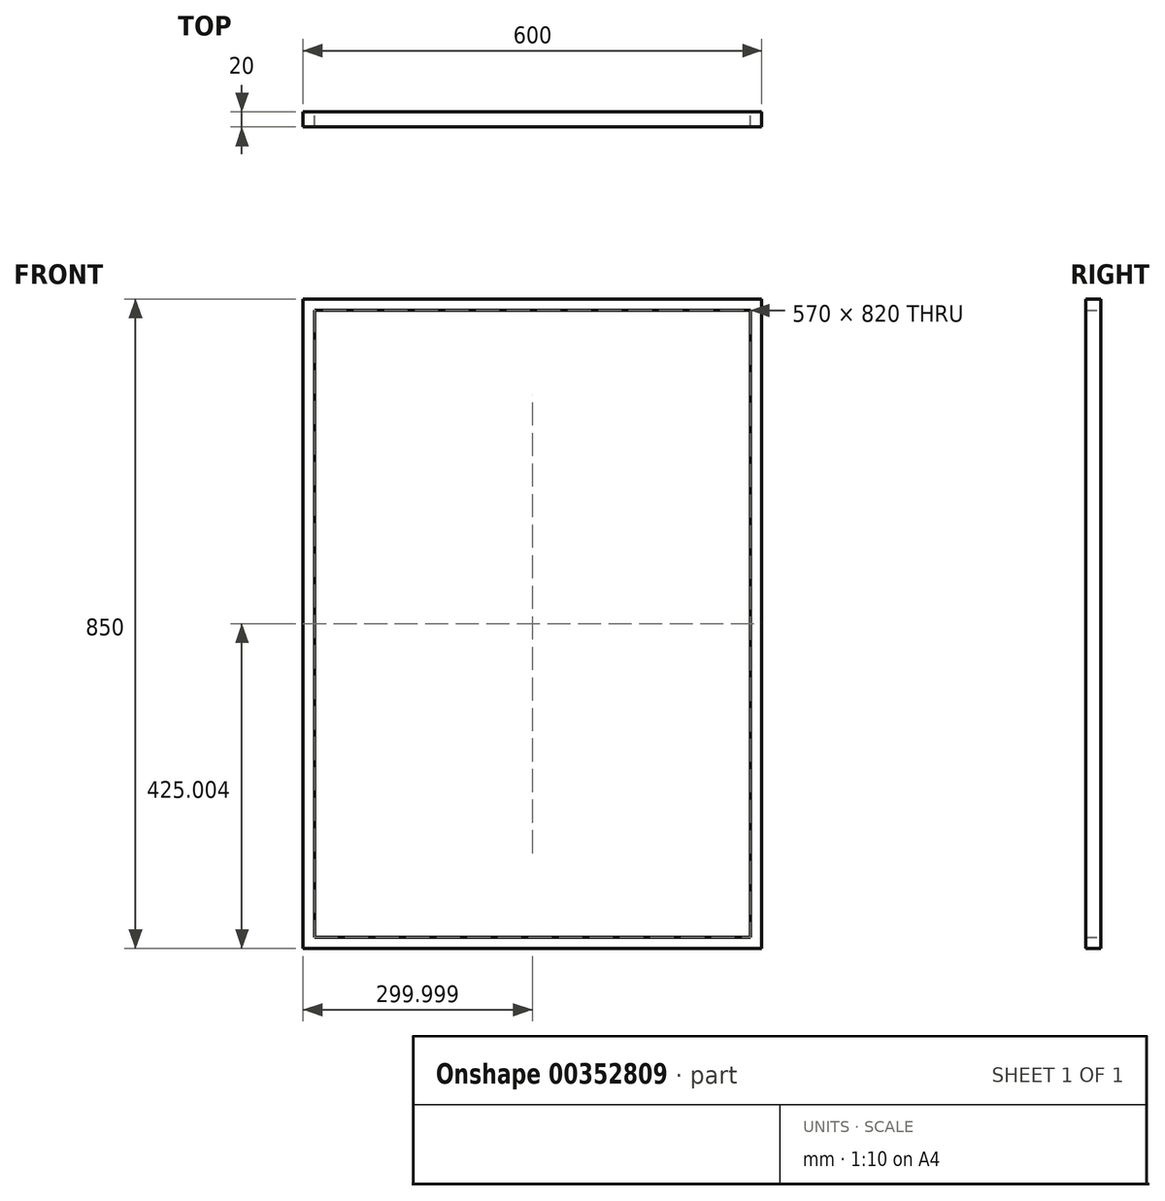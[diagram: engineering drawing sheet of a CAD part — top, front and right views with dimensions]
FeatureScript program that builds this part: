
annotation { "Feature Type Name" : "Feature", "Feature Type Description" : "" }
export const myFeature = defineFeature(function(context is Context, id is Id, definition is map)
    precondition{}
    {
        {
            var Q0;
            Q0=qCreatedBy(makeId("Front.planeOp"),FACE);
            var sketch = newSketch(context, id + "F0", { "sketchPlane" : qUnion([Q0])});
            skLineSegment(sketch, "E0.bottom", {"start": v(-39.41, 785.08) * mm, "end": v(560.59, 785.08) * mm});
            skLineSegment(sketch, "E0.top", {"start": v(-39.41, -64.92) * mm, "end": v(560.59, -64.92) * mm});
            skLineSegment(sketch, "E0.left", {"start": v(-39.41, 785.08) * mm, "end": v(-39.41, -64.92) * mm});
            skLineSegment(sketch, "E0.right", {"start": v(560.59, 785.08) * mm, "end": v(560.59, -64.92) * mm});
            skLineSegment(sketch, "E1.0", {"start": v(-24.41, 770.08) * mm, "end": v(545.59, 770.08) * mm});
            skLineSegment(sketch, "E1.1", {"start": v(-24.41, 770.08) * mm, "end": v(-24.41, -49.92) * mm});
            skLineSegment(sketch, "E1.2", {"start": v(-24.41, -49.92) * mm, "end": v(545.59, -49.92) * mm});
            skLineSegment(sketch, "E1.3", {"start": v(545.59, 770.08) * mm, "end": v(545.59, -49.92) * mm});
            skSolve(sketch);
        }
        {
            var Q0;
            Q0=qSketchRegion(id+"F0",true);
            extrude(context, id + "F1", {"entities" : qUnion([Q0]), "depth" : 20 * mm});
        }
        {
            var Q0;
            Q0=makeQuery(id+"F1.opExtrude","CAP_FACE",FACE,{"disambiguationData":[OSD([sQuery(id+"F0.wireOp",EDGE,"E0.bottom"),sQuery(id+"F0.wireOp",EDGE,"E0.top"),sQuery(id+"F0.wireOp",EDGE,"E0.left"),sQuery(id+"F0.wireOp",EDGE,"E0.right"),sQuery(id+"F0.wireOp",EDGE,"E1.0"),sQuery(id+"F0.wireOp",EDGE,"E1.1"),sQuery(id+"F0.wireOp",EDGE,"E1.2"),sQuery(id+"F0.wireOp",EDGE,"E1.3")])],"isStart":false});
            var sketch = newSketch(context, id + "F2", { "sketchPlane" : qUnion([Q0])});
            skLineSegment(sketch, "E2.bottom", {"start": v(-39.41, 785.08) * mm, "end": v(560.59, 785.08) * mm});
            skLineSegment(sketch, "E2.top", {"start": v(-39.41, -64.92) * mm, "end": v(560.59, -64.92) * mm});
            skLineSegment(sketch, "E2.left", {"start": v(-39.41, 785.08) * mm, "end": v(-39.41, -64.92) * mm});
            skLineSegment(sketch, "E2.right", {"start": v(560.59, 785.08) * mm, "end": v(560.59, -64.92) * mm});
            skSolve(sketch);
        }
        {
            var Q0;
            Q0=qSketchRegion(id+"F2",true);
            extrude(context, id + "F3", {"entities" : qUnion([Q0]), "operationType" : NewBodyOperationType.ADD, "oppositeDirection" : true, "depth" : 5 * mm});
        }
        {
            var Q0;
            Q0=makeQuery(id+"F3.opExtrude","CAP_FACE",FACE,{"disambiguationData":[OSD([sQuery(id+"F2.wireOp",EDGE,"E2.bottom"),sQuery(id+"F2.wireOp",EDGE,"E2.top"),sQuery(id+"F2.wireOp",EDGE,"E2.left"),sQuery(id+"F2.wireOp",EDGE,"E2.right")])],"isStart":false});
            var sketch = newSketch(context, id + "F4", { "sketchPlane" : qUnion([Q0])});
            skLineSegment(sketch, "E3.bottom", {"start": v(-545.59, 770.08) * mm, "end": v(24.41, 770.08) * mm});
            skLineSegment(sketch, "E3.top", {"start": v(-545.59, -49.92) * mm, "end": v(24.41, -49.92) * mm});
            skLineSegment(sketch, "E3.left", {"start": v(-545.59, 770.08) * mm, "end": v(-545.59, -49.92) * mm});
            skLineSegment(sketch, "E3.right", {"start": v(24.41, 770.08) * mm, "end": v(24.41, -49.92) * mm});
            skSolve(sketch);
        }
        {
            var Q0;
            Q0=qSketchRegion(id+"F4",true);
            extrude(context, id + "F5", {"entities" : qUnion([Q0]), "operationType" : NewBodyOperationType.REMOVE, "oppositeDirection" : true, "depth" : 25 * mm});
        }
    });
